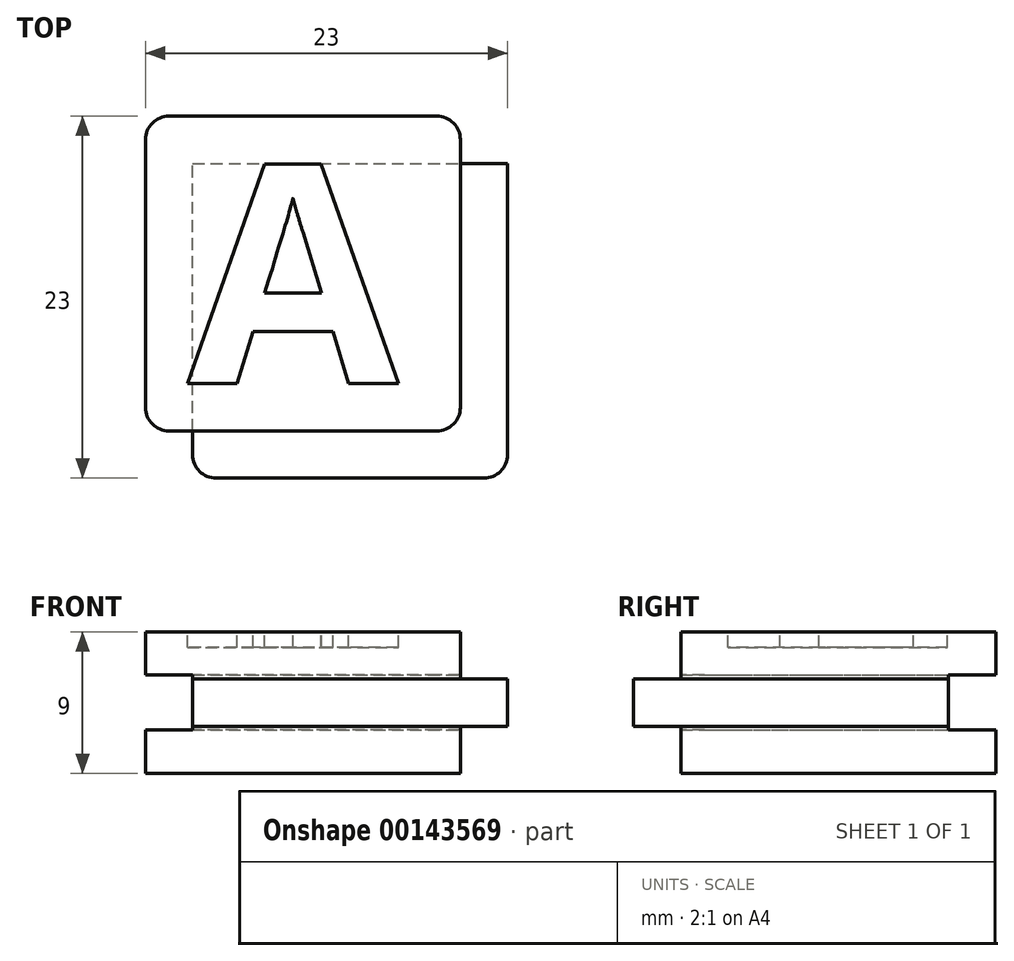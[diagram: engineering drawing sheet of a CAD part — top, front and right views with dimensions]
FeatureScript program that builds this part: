
annotation { "Feature Type Name" : "Feature", "Feature Type Description" : "" }
export const myFeature = defineFeature(function(context is Context, id is Id, definition is map)
    precondition{}
    {
        {
            var Q0;
            Q0=qCreatedBy(makeId("Front.planeOp"),FACE);
            var sketch = newSketch(context, id + "F0", { "sketchPlane" : qUnion([Q0])});
            skLineSegment(sketch, "E0.bottom", {"start": v(10, 4.5) * mm, "end": v(-10, 4.5) * mm});
            skLineSegment(sketch, "E0.top", {"start": v(10, -4.5) * mm, "end": v(-10, -4.5) * mm});
            skLineSegment(sketch, "E0.left", {"start": v(10, 4.5) * mm, "end": v(10, -4.5) * mm});
            skLineSegment(sketch, "E0.right", {"start": v(-10, 4.5) * mm, "end": v(-10, -4.5) * mm});
            skPoint(sketch, "E0.middle", {"position": v(0, 0) * mm});
            skLineSegment(sketch, "E1.bottom", {"start": v(13, 1.5) * mm, "end": v(7, 1.5) * mm});
            skLineSegment(sketch, "E1.top", {"start": v(13, -1.5) * mm, "end": v(7, -1.5) * mm});
            skLineSegment(sketch, "E1.left", {"start": v(13, 1.5) * mm, "end": v(13, -1.5) * mm});
            skLineSegment(sketch, "E1.right", {"start": v(7, 1.5) * mm, "end": v(7, -1.5) * mm});
            skPoint(sketch, "E1.middle", {"position": v(10, 0) * mm});
            skLineSegment(sketch, "E2.bottom", {"start": v(7, 1.5) * mm, "end": v(-7, 1.5) * mm});
            skLineSegment(sketch, "E2.top", {"start": v(7, -1.5) * mm, "end": v(-7, -1.5) * mm});
            skLineSegment(sketch, "E2.right", {"start": v(-7, 1.5) * mm, "end": v(-7, -1.5) * mm});
            skLineSegment(sketch, "E3.bottom", {"start": v(-7, -1.5) * mm, "end": v(-10, -1.5) * mm});
            skLineSegment(sketch, "E3.top", {"start": v(-7, 1.5) * mm, "end": v(-10, 1.5) * mm});
            skLineSegment(sketch, "E3.left", {"start": v(-7, -1.5) * mm, "end": v(-7, 1.5) * mm});
            skLineSegment(sketch, "E3.right", {"start": v(-10, -1.5) * mm, "end": v(-10, 1.5) * mm});
            skSolve(sketch);
        }
        {
            var Q0;
            {var subQ5=sQuery(id+"F0.wireOp",EDGE,"E0.bottom");Q0=makeQuery(id+"F0.imprint","IMPRINT",FACE,{"disambiguationData":[TD([[makeQuery(id+"F0.imprint","IMPRINT",EDGE,{"derivedFrom":subQ5}),1.0]])]});}
            var Q1;
            Q1=makeQuery(id+"F0.imprint","IMPRINT",FACE,{"disambiguationData":[TD([[makeQuery(id+"F0.imprint","IMPRINT",EDGE,{"derivedFrom":sQuery(id+"F0.wireOp",EDGE,"E2.bottom")}),1.0]])]});
            var Q2;
            {var subQ5=sQuery(id+"F0.wireOp",EDGE,"E1.left");Q2=makeQuery(id+"F0.imprint","IMPRINT",FACE,{"disambiguationData":[TD([[makeQuery(id+"F0.imprint","IMPRINT",EDGE,{"derivedFrom":subQ5}),-1.0]])]});}
            var Q3;
            {var subQ5=sQuery(id+"F0.wireOp",EDGE,"E1.right");Q3=makeQuery(id+"F0.imprint","IMPRINT",FACE,{"disambiguationData":[TD([[makeQuery(id+"F0.imprint","IMPRINT",EDGE,{"derivedFrom":subQ5}),1.0]])]});}
            var Q4;
            Q4=makeQuery(id+"F0.imprint","IMPRINT",FACE,{"disambiguationData":[TD([[makeQuery(id+"F0.imprint","IMPRINT",EDGE,{"derivedFrom":sQuery(id+"F0.wireOp",EDGE,"E3.bottom")}),-1.0]])]});
            var Q5;
            {var subQ5=sQuery(id+"F0.wireOp",EDGE,"E0.top");Q5=makeQuery(id+"F0.imprint","IMPRINT",FACE,{"disambiguationData":[TD([[makeQuery(id+"F0.imprint","IMPRINT",EDGE,{"derivedFrom":subQ5}),-1.0]])]});}
            extrude(context, id + "F1", {"entities" : qUnion([Q0, Q1, Q2, Q3, Q4, Q5]), "oppositeDirection" : true, "depth" : 20 * mm});
        }
        {
            var Q0;
            Q0=makeQuery(id+"F0.imprint","IMPRINT",FACE,{"disambiguationData":[TD([[makeQuery(id+"F0.imprint","IMPRINT",EDGE,{"derivedFrom":sQuery(id+"F0.wireOp",EDGE,"E3.bottom")}),-1.0]])]});
            var Q1;
            Q1=makeQuery(id+"F0.imprint","IMPRINT",FACE,{"disambiguationData":[TD([[makeQuery(id+"F0.imprint","IMPRINT",EDGE,{"derivedFrom":sQuery(id+"F0.wireOp",EDGE,"E2.bottom")}),1.0]])]});
            var Q2;
            {var subQ5=sQuery(id+"F0.wireOp",EDGE,"E1.right");Q2=makeQuery(id+"F0.imprint","IMPRINT",FACE,{"disambiguationData":[TD([[makeQuery(id+"F0.imprint","IMPRINT",EDGE,{"derivedFrom":subQ5}),1.0]])]});}
            var Q3;
            {var subQ5=sQuery(id+"F0.wireOp",EDGE,"E1.left");Q3=makeQuery(id+"F0.imprint","IMPRINT",FACE,{"disambiguationData":[TD([[makeQuery(id+"F0.imprint","IMPRINT",EDGE,{"derivedFrom":subQ5}),-1.0]])]});}
            extrude(context, id + "F2", {"entities" : qUnion([Q0, Q1, Q2, Q3]), "operationType" : NewBodyOperationType.ADD, "depth" : 3 * mm});
        }
        {
            var Q0;
            {var subQ0=sQuery(id+"F0.wireOp",EDGE,"E1.left");Q0=makeQuery(id+"F2.boolean.opBoolean","MERGE",FACE,{"derivedFrom":[makeQuery(id+"F1.opExtrude","SWEPT_FACE",FACE,{"disambiguationData":[OSD([subQ0])]}),makeQuery(id+"F2.opExtrude","SWEPT_FACE",FACE,{"disambiguationData":[OSD([subQ0])]})]});}
            var sketch = newSketch(context, id + "F3", { "sketchPlane" : qUnion([Q0])});
            skLineSegment(sketch, "E4.bottom", {"start": v(23, 1.75) * mm, "end": v(17, 1.75) * mm});
            skLineSegment(sketch, "E4.top", {"start": v(23, -1.75) * mm, "end": v(17, -1.75) * mm});
            skLineSegment(sketch, "E4.left", {"start": v(23, 1.75) * mm, "end": v(23, -1.75) * mm});
            skLineSegment(sketch, "E4.right", {"start": v(17, 1.75) * mm, "end": v(17, -1.75) * mm});
            skPoint(sketch, "E4.middle", {"position": v(20, 0) * mm});
            skSolve(sketch);
        }
        {
            var Q0;
            {var subQ1=sQuery(id+"F3.wireOp",EDGE,"E4.bottom");Q0=makeQuery(id+"F3.imprint","IMPRINT",FACE,{"disambiguationData":[TD([[makeQuery(id+"F3.imprint","IMPRINT",EDGE,{"derivedFrom":subQ1}),1.0]])]});}
            var Q1;
            {var subQ1=sQuery(id+"F0.wireOp",EDGE,"E1.left");var subQ8=makeQuery(id+"F1.opExtrude","CAP_EDGE",EDGE,{"disambiguationData":[OSD([subQ1])],"isStart":false});Q1=makeQuery(id+"F3.imprint","IMPRINT",FACE,{"disambiguationData":[TD([[makeQuery(id+"F3.imprint","IMPRINT",EDGE,{"derivedFrom":subQ8}),-1.0]])]});}
            extrude(context, id + "F4", {"entities" : qUnion([Q0, Q1]), "operationType" : NewBodyOperationType.REMOVE, "oppositeDirection" : true, "depth" : 100 * mm});
        }
        {
            var Q0;
            Q0=makeQuery(id+"F4.boolean.opBoolean","COPY",FACE,{"derivedFrom":makeQuery(id+"F4.opExtrude","SWEPT_FACE",FACE,{"disambiguationData":[OSD([sQuery(id+"F3.wireOp",EDGE,"E4.right")])]})});
            var sketch = newSketch(context, id + "F5", { "sketchPlane" : qUnion([Q0])});
            skLineSegment(sketch, "E5.bottom", {"start": v(13, 1.75) * mm, "end": v(7, 1.75) * mm});
            skLineSegment(sketch, "E5.top", {"start": v(13, -1.75) * mm, "end": v(7, -1.75) * mm});
            skLineSegment(sketch, "E5.left", {"start": v(13, 1.75) * mm, "end": v(13, -1.75) * mm});
            skLineSegment(sketch, "E5.right", {"start": v(7, 1.75) * mm, "end": v(7, -1.75) * mm});
            skPoint(sketch, "E5.middle", {"position": v(10, 0) * mm});
            skSolve(sketch);
        }
        {
            var Q0;
            {var subQ3=sQuery(id+"F5.wireOp",EDGE,"E5.left");Q0=makeQuery(id+"F5.imprint","IMPRINT",FACE,{"disambiguationData":[TD([[makeQuery(id+"F5.imprint","IMPRINT",EDGE,{"derivedFrom":subQ3}),-1.0]])]});}
            var Q1;
            {var subQ4=sQuery(id+"F5.wireOp",EDGE,"E5.right");Q1=makeQuery(id+"F5.imprint","IMPRINT",FACE,{"disambiguationData":[TD([[makeQuery(id+"F5.imprint","IMPRINT",EDGE,{"derivedFrom":subQ4}),1.0]])]});}
            extrude(context, id + "F6", {"entities" : qUnion([Q0, Q1]), "operationType" : NewBodyOperationType.REMOVE, "oppositeDirection" : true, "depth" : 100 * mm});
        }
        {
            var Q0;
            Q0=makeQuery(id+"F6.boolean.opBoolean","INTERSECT",EDGE,{"derivedFrom":[makeQuery(id+"F2.opExtrude","CAP_FACE",FACE,{"disambiguationData":[OSD([sQuery(id+"F0.wireOp",EDGE,"E1.bottom"),sQuery(id+"F0.wireOp",EDGE,"E1.top"),sQuery(id+"F0.wireOp",EDGE,"E1.left"),sQuery(id+"F0.wireOp",EDGE,"E2.bottom"),sQuery(id+"F0.wireOp",EDGE,"E2.top"),sQuery(id+"F0.wireOp",EDGE,"E3.bottom"),sQuery(id+"F0.wireOp",EDGE,"E3.top"),sQuery(id+"F0.wireOp",EDGE,"E3.right")])],"isStart":false}),makeQuery(id+"F6.opExtrude","SWEPT_FACE",FACE,{"disambiguationData":[OSD([sQuery(id+"F5.wireOp",EDGE,"E5.right")])]})]});
            var Q1;
            Q1=makeQuery(id+"F2.opExtrude","CAP_EDGE",EDGE,{"disambiguationData":[OSD([sQuery(id+"F0.wireOp",EDGE,"E1.left")])],"isStart":false});
            var Q2;
            {var subQ0=sQuery(id+"F0.wireOp",EDGE,"E0.left");Q2=makeQuery(id+"F1.opExtrude","CAP_EDGE",EDGE,{"disambiguationData":[OSD([subQ0]),TDD([makeQuery(id+"F0.imprint","IMPRINT",EDGE,{"disambiguationData":[TD([[makeQuery(id+"F0.imprint","INTERSECT",VERTEX,{"derivedFrom":[sQuery(id+"F0.wireOp",EDGE,"E0.bottom"),subQ0]}),-1.0]])],"derivedFrom":subQ0})])],"isStart":true});}
            var Q3;
            {var subQ0=sQuery(id+"F0.wireOp",EDGE,"E0.left");Q3=makeQuery(id+"F1.opExtrude","CAP_EDGE",EDGE,{"disambiguationData":[OSD([subQ0]),TDD([makeQuery(id+"F0.imprint","IMPRINT",EDGE,{"disambiguationData":[TD([[makeQuery(id+"F0.imprint","INTERSECT",VERTEX,{"derivedFrom":[sQuery(id+"F0.wireOp",EDGE,"E0.top"),subQ0]}),1.0]])],"derivedFrom":subQ0})])],"isStart":true});}
            var Q4;
            {var subQ0=sQuery(id+"F0.wireOp",EDGE,"E3.right");var subQ1=sQuery(id+"F0.wireOp",EDGE,"E0.right");var subQ3=sQuery(id+"F0.wireOp",EDGE,"E0.top");Q4=makeQuery(id+"F2.boolean.opBoolean","SPLIT",EDGE,{"disambiguationData":[TD([makeQuery(id+"F1.opExtrude","SWEPT_FACE",FACE,{"disambiguationData":[OSD([subQ3])]})])],"derivedFrom":makeQuery(id+"F1.opExtrude","CAP_EDGE",EDGE,{"disambiguationData":[OSD([subQ1,subQ0])],"isStart":true})});}
            var Q5;
            {var subQ1=sQuery(id+"F0.wireOp",EDGE,"E3.right");var subQ2=sQuery(id+"F0.wireOp",EDGE,"E0.right");var subQ3=sQuery(id+"F0.wireOp",EDGE,"E0.bottom");Q5=makeQuery(id+"F2.boolean.opBoolean","SPLIT",EDGE,{"disambiguationData":[TD([makeQuery(id+"F1.opExtrude","SWEPT_FACE",FACE,{"disambiguationData":[OSD([subQ3])]})])],"derivedFrom":makeQuery(id+"F1.opExtrude","CAP_EDGE",EDGE,{"disambiguationData":[OSD([subQ2,subQ1])],"isStart":true})});}
            var Q6;
            Q6=makeQuery(id+"F6.boolean.opBoolean","COPY",EDGE,{"derivedFrom":makeQuery(id+"F6.opExtrude","CAP_EDGE",EDGE,{"disambiguationData":[OSD([sQuery(id+"F5.wireOp",EDGE,"E5.right")])],"isStart":true})});
            var Q7;
            {var subQ0=sQuery(id+"F0.wireOp",EDGE,"E3.right");var subQ1=sQuery(id+"F0.wireOp",EDGE,"E0.right");var subQ2=sQuery(id+"F0.wireOp",EDGE,"E0.bottom");Q7=makeQuery(id+"F4.boolean.opBoolean","SPLIT",EDGE,{"disambiguationData":[TD([makeQuery(id+"F1.opExtrude","SWEPT_FACE",FACE,{"disambiguationData":[OSD([subQ2])]})])],"derivedFrom":makeQuery(id+"F1.opExtrude","CAP_EDGE",EDGE,{"disambiguationData":[OSD([subQ1,subQ0])],"isStart":false})});}
            var Q8;
            {var subQ0=sQuery(id+"F0.wireOp",EDGE,"E3.right");var subQ1=sQuery(id+"F0.wireOp",EDGE,"E0.right");var subQ2=sQuery(id+"F0.wireOp",EDGE,"E0.top");Q8=makeQuery(id+"F4.boolean.opBoolean","SPLIT",EDGE,{"disambiguationData":[TD([makeQuery(id+"F1.opExtrude","SWEPT_FACE",FACE,{"disambiguationData":[OSD([subQ2])]})])],"derivedFrom":makeQuery(id+"F1.opExtrude","CAP_EDGE",EDGE,{"disambiguationData":[OSD([subQ1,subQ0])],"isStart":false})});}
            var Q9;
            Q9=makeQuery(id+"F4.boolean.opBoolean","COPY",EDGE,{"derivedFrom":makeQuery(id+"F4.opExtrude","CAP_EDGE",EDGE,{"disambiguationData":[OSD([sQuery(id+"F3.wireOp",EDGE,"E4.right")])],"isStart":true})});
            var Q10;
            {var subQ0=sQuery(id+"F0.wireOp",EDGE,"E0.left");Q10=makeQuery(id+"F1.opExtrude","CAP_EDGE",EDGE,{"disambiguationData":[OSD([subQ0]),TDD([makeQuery(id+"F0.imprint","IMPRINT",EDGE,{"disambiguationData":[TD([[makeQuery(id+"F0.imprint","INTERSECT",VERTEX,{"derivedFrom":[sQuery(id+"F0.wireOp",EDGE,"E0.bottom"),subQ0]}),-1.0]])],"derivedFrom":subQ0})])],"isStart":false});}
            var Q11;
            {var subQ0=sQuery(id+"F0.wireOp",EDGE,"E0.left");Q11=makeQuery(id+"F1.opExtrude","CAP_EDGE",EDGE,{"disambiguationData":[OSD([subQ0]),TDD([makeQuery(id+"F0.imprint","IMPRINT",EDGE,{"disambiguationData":[TD([[makeQuery(id+"F0.imprint","INTERSECT",VERTEX,{"derivedFrom":[sQuery(id+"F0.wireOp",EDGE,"E0.top"),subQ0]}),1.0]])],"derivedFrom":subQ0})])],"isStart":false});}
            fillet(context, id + "F7", {"entities" : qUnion([Q0, Q1, Q2, Q3, Q4, Q5, Q6, Q7, Q8, Q9, Q10, Q11]), "radius" : 1.5 * mm, "tangentPropagation" : true, "allowEdgeOverflow" : false});
        }
        {
            var Q0;
            Q0=makeQuery(id+"F1.opExtrude","SWEPT_FACE",FACE,{"disambiguationData":[OSD([sQuery(id+"F0.wireOp",EDGE,"E0.bottom")])]});
            var sketch = newSketch(context, id + "F8", { "sketchPlane" : qUnion([Q0])});
            skLineSegment(sketch, "E6", {"start": v(0, 20) * mm, "end": v(0, 0) * mm});
            skLineSegment(sketch, "E7.bottom", {"start": v(7.34, 17) * mm, "end": v(-7.34, 17) * mm});
            skLineSegment(sketch, "E7.top", {"start": v(7.34, 3) * mm, "end": v(-7.34, 3) * mm});
            skLineSegment(sketch, "E7.left", {"start": v(7.34, 17) * mm, "end": v(7.34, 3) * mm});
            skLineSegment(sketch, "E7.right", {"start": v(-7.34, 17) * mm, "end": v(-7.34, 3) * mm});
            skPoint(sketch, "E7.middle", {"position": v(0, 10) * mm});
            skText(sketch, "E8", { "text": "A", "fontName": "OpenSans-Bold.ttf"});
            const initialGuessF8  = {"E8": [-0.00734, 0.003, 1, 0, 0.014]};
            skSetInitialGuess(sketch, initialGuessF8);
            skSolve(sketch);
        }
        {
            var Q0;
            {var subQ7=sQuery(id+"F8.wireOp",EDGE,"E8.sketch_text.stroke-2");Q0=makeQuery(id+"F8.imprint","IMPRINT",FACE,{"disambiguationData":[TD([[makeQuery(id+"F8.imprint","IMPRINT",EDGE,{"derivedFrom":subQ7}),-1.0]])]});}
            var Q1;
            {var subQ1=sQuery(id+"F8.wireOp",EDGE,"E8.sketch_text.stroke-0");Q1=makeQuery(id+"F8.imprint","IMPRINT",FACE,{"disambiguationData":[TD([[makeQuery(id+"F8.imprint","IMPRINT",EDGE,{"derivedFrom":subQ1}),-1.0]])]});}
            extrude(context, id + "F9", {"entities" : qUnion([Q0, Q1]), "operationType" : NewBodyOperationType.REMOVE, "oppositeDirection" : true, "depth" : 1 * mm});
        }
    });
